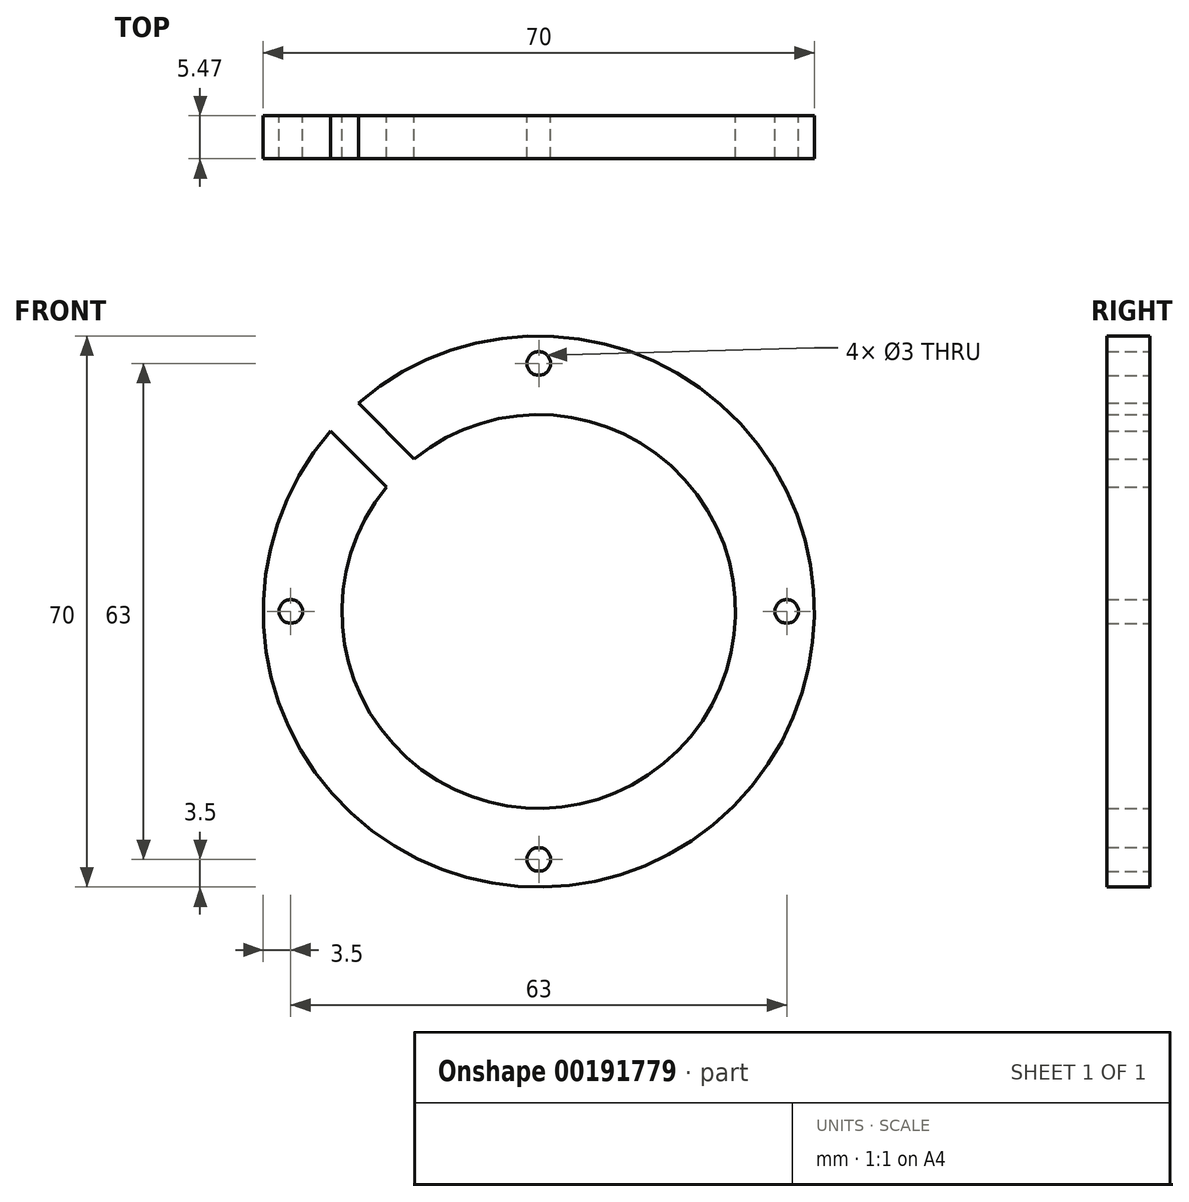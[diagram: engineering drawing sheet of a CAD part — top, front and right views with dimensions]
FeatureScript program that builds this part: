
annotation { "Feature Type Name" : "Feature", "Feature Type Description" : "" }
export const myFeature = defineFeature(function(context is Context, id is Id, definition is map)
    precondition{}
    {
        {
            var Q0;
            Q0=qCreatedBy(makeId("Front.planeOp"),FACE);
            var sketch = newSketch(context, id + "F0", { "sketchPlane" : qUnion([Q0])});
            skArc(sketch, "E0", {"start": v(-19.36, 15.82) * mm, "mid": v(17.68, -17.68) * mm, "end": v(-15.82, 19.36) * mm});
            skArc(sketch, "E1", {"start": v(-26.45, 22.92) * mm, "mid": v(24.75, -24.75) * mm, "end": v(-22.92, 26.45) * mm});
            skCircle(sketch, "E2", {"center": v(0, 0) * mm, "radius": 31.5 * mm, "construction": true});
            skCircle(sketch, "E3", {"center": v(0, 31.5) * mm, "radius": 1.5 * mm});
            skCircle(sketch, "E4.1.0", {"center": v(-31.5, 0) * mm, "radius": 1.5 * mm});
            skCircle(sketch, "E4.2.0", {"center": v(0, -31.5) * mm, "radius": 1.5 * mm});
            skCircle(sketch, "E4.3.0", {"center": v(31.5, 0) * mm, "radius": 1.5 * mm});
            skLineSegment(sketch, "E5", {"start": v(-26.45, 22.92) * mm, "end": v(-19.36, 15.82) * mm});
            skLineSegment(sketch, "E6", {"start": v(-15.82, 19.36) * mm, "end": v(-22.92, 26.45) * mm});
            skLineSegment(sketch, "E7", {"start": v(-35.63, 0) * mm, "end": v(32.67, 0) * mm, "construction": true});
            skLineSegment(sketch, "E8", {"start": v(0, 0) * mm, "end": v(-23.44, 23.44) * mm, "construction": true});
            skSolve(sketch);
        }
        {
            var Q0;
            Q0=makeQuery(id+"F0.imprint","IMPRINT",FACE,{"disambiguationData":[TD([[makeQuery(id+"F0.imprint","IMPRINT",EDGE,{"derivedFrom":sQuery(id+"F0.wireOp",EDGE,"E0")}),-1.0]])]});
            extrude(context, id + "F1", {"entities" : qUnion([Q0]), "depth" : 5.47 * mm});
        }
    });
